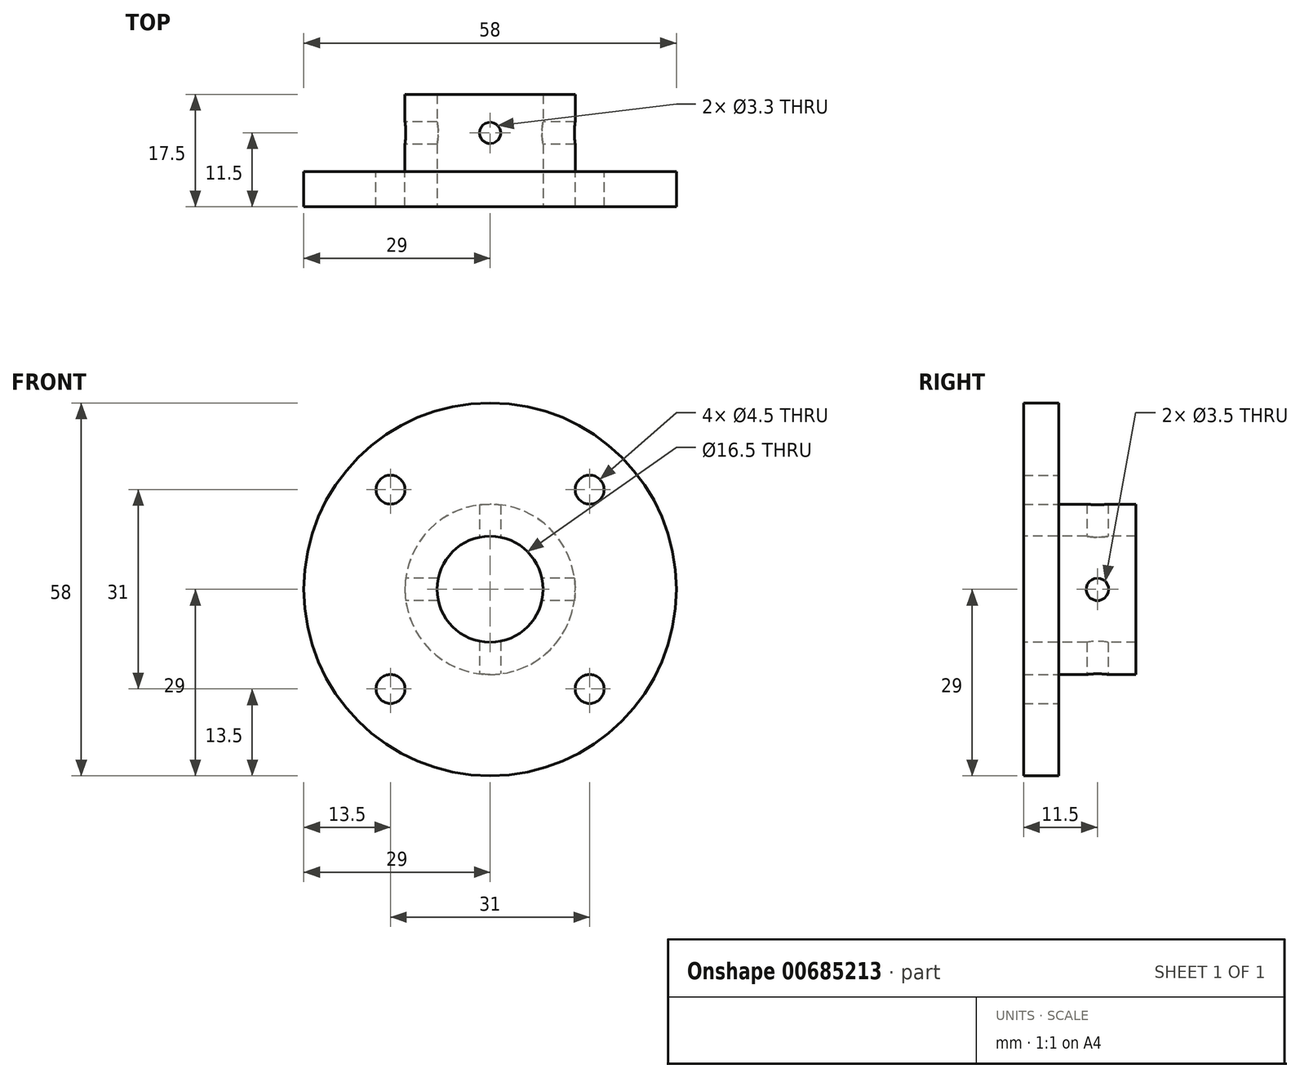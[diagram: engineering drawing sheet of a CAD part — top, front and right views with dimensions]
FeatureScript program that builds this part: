
annotation { "Feature Type Name" : "Feature", "Feature Type Description" : "" }
export const myFeature = defineFeature(function(context is Context, id is Id, definition is map)
    precondition{}
    {
        {
            var Q0;
            Q0=qCreatedBy(makeId("Right.planeOp"),FACE);
            var sketch = newSketch(context, id + "F0", { "sketchPlane" : qUnion([Q0])});
            skLineSegment(sketch, "E0", {"start": v(0, 8.25) * mm, "end": v(0, 29) * mm});
            skLineSegment(sketch, "E1", {"start": v(0, 29) * mm, "end": v(5.5, 29) * mm});
            skLineSegment(sketch, "E2", {"start": v(5.5, 29) * mm, "end": v(5.5, 13.25) * mm});
            skLineSegment(sketch, "E3", {"start": v(5.5, 13.25) * mm, "end": v(17.5, 13.25) * mm});
            skLineSegment(sketch, "E4", {"start": v(17.5, 13.25) * mm, "end": v(17.5, 8.25) * mm});
            skLineSegment(sketch, "E5", {"start": v(17.5, 8.25) * mm, "end": v(0, 8.25) * mm});
            skLineSegment(sketch, "E6", {"start": v(0, 0) * mm, "end": v(10.68, 0) * mm});
            skLineSegment(sketch, "E7.MirrorCS", {"start": v(0, -29) * mm, "end": v(5.5, -29) * mm});
            skLineSegment(sketch, "E8.MirrorCS", {"start": v(5.5, -29) * mm, "end": v(5.5, -13.25) * mm});
            skLineSegment(sketch, "E9.MirrorCS", {"start": v(17.5, -13.25) * mm, "end": v(17.5, -8.25) * mm});
            skLineSegment(sketch, "E10.MirrorCS", {"start": v(0, -8.25) * mm, "end": v(0, -29) * mm});
            skLineSegment(sketch, "E11.MirrorCS", {"start": v(17.5, -8.25) * mm, "end": v(0, -8.25) * mm});
            skLineSegment(sketch, "E12.MirrorCS", {"start": v(5.5, -13.25) * mm, "end": v(17.5, -13.25) * mm});
            skSolve(sketch);
        }
        {
            var Q0;
            Q0=makeQuery(id+"F0.imprint","IMPRINT",FACE,{"disambiguationData":[TD([[makeQuery(id+"F0.imprint","IMPRINT",EDGE,{"derivedFrom":sQuery(id+"F0.wireOp",EDGE,"E0")}),-1.0]])]});
            var Q1;
            Q1=sQuery(id+"F0.wireOp",EDGE,"E6");
            revolve(context, id + "F1", {"entities" : qUnion([Q0]), "axis" : qUnion([Q1]), "revolveType" : RevolveType.FULL});
        }
        {
            var Q0;
            Q0=makeQuery(id+"F1.opRevolve","SWEPT_EDGE",EDGE,{"disambiguationData":[OSD([sQuery(id+"F0.wireOp",EDGE,"E2"),sQuery(id+"F0.wireOp",EDGE,"E3")])]});
            fillet(context, id + "F2", {"entities" : qUnion([Q0]), "radius" : 0.25 * mm, "tangentPropagation" : true, "allowEdgeOverflow" : false});
        }
        {
            var Q0;
            Q0=makeQuery(id+"F1.opRevolve","SWEPT_FACE",FACE,{"disambiguationData":[OSD([sQuery(id+"F0.wireOp",EDGE,"E2")])]});
            var sketch = newSketch(context, id + "F3", { "sketchPlane" : qUnion([Q0])});
            skCircle(sketch, "E13", {"center": v(-15.5, 15.5) * mm, "radius": 2.25 * mm});
            skCircle(sketch, "E14", {"center": v(15.5, 15.5) * mm, "radius": 2.25 * mm});
            skCircle(sketch, "E15", {"center": v(-15.5, -15.5) * mm, "radius": 2.25 * mm});
            skCircle(sketch, "E16", {"center": v(15.5, -15.5) * mm, "radius": 2.25 * mm});
            skSolve(sketch);
        }
        {
            var Q0;
            Q0 = qSketchRegion(id + "F3", true);
            extrude(context, id + "F4", {"entities" : qUnion([Q0]), "operationType" : NewBodyOperationType.REMOVE, "oppositeDirection" : true, "depth" : 25 * mm, "offsetDistance" : 25 * mm});
        }
        {
            var Q0;
            Q0=qCreatedBy(makeId("Top.planeOp"),FACE);
            var sketch = newSketch(context, id + "F5", { "sketchPlane" : qUnion([Q0])});
            skCircle(sketch, "E17", {"center": v(0, 11.5) * mm, "radius": 1.65 * mm});
            skSolve(sketch);
        }
        {
            var Q0;
            Q0 = qSketchRegion(id + "F5", true);
            extrude(context, id + "F6", {"entities" : qUnion([Q0]), "operationType" : NewBodyOperationType.REMOVE, "depth" : 25 * mm, "offsetDistance" : 25 * mm, "hasSecondDirection" : true, "secondDirectionOppositeDirection" : true, "secondDirectionDepth" : 25 * mm});
        }
        {
            var Q0;
            Q0=qCreatedBy(makeId("Right.planeOp"),FACE);
            var sketch = newSketch(context, id + "F7", { "sketchPlane" : qUnion([Q0])});
            skCircle(sketch, "E18", {"center": v(11.5, 0) * mm, "radius": 1.75 * mm});
            skSolve(sketch);
        }
        {
            var Q0;
            Q0 = qSketchRegion(id + "F7", true);
            extrude(context, id + "F8", {"entities" : qUnion([Q0]), "operationType" : NewBodyOperationType.REMOVE, "depth" : 25 * mm, "offsetDistance" : 25 * mm, "hasSecondDirection" : true, "secondDirectionOppositeDirection" : true, "secondDirectionDepth" : 25 * mm});
        }
    });
